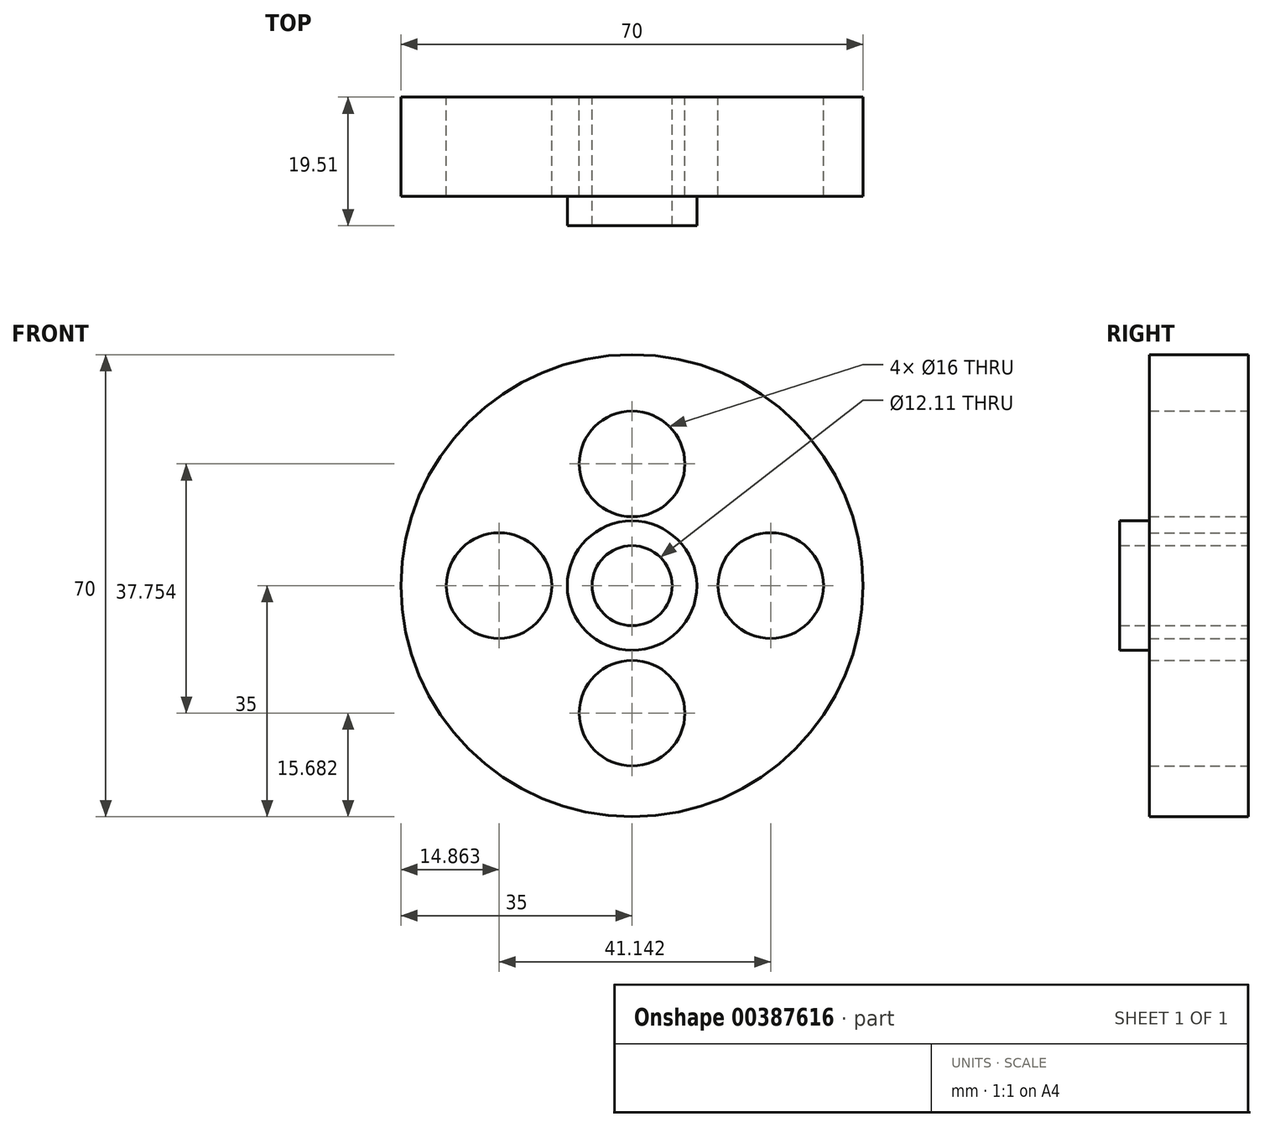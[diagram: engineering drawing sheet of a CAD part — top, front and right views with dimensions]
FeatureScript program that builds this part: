
annotation { "Feature Type Name" : "Feature", "Feature Type Description" : "" }
export const myFeature = defineFeature(function(context is Context, id is Id, definition is map)
    precondition{}
    {
        {
            var Q0;
            Q0=qCreatedBy(makeId("Front.planeOp"),FACE);
            var sketch = newSketch(context, id + "F0", { "sketchPlane" : qUnion([Q0])});
            skCircle(sketch, "E0", {"center": v(0, 0) * mm, "radius": 30 * mm});
            skCircle(sketch, "E1", {"center": v(0, 0) * mm, "radius": 35 * mm});
            skCircle(sketch, "E2", {"center": v(0, 0) * mm, "radius": 6.06 * mm});
            skCircle(sketch, "E3", {"center": v(0, 0) * mm, "radius": 9.81 * mm});
            skPoint(sketch, "E4", {"position": v(0, 18.44) * mm});
            skCircle(sketch, "E5", {"center": v(0, 18.44) * mm, "radius": 8 * mm});
            skPoint(sketch, "E6", {"position": v(21, 0) * mm});
            skCircle(sketch, "E7", {"center": v(21, 0) * mm, "radius": 8 * mm});
            skCircle(sketch, "E8", {"center": v(0, -19.32) * mm, "radius": 8 * mm});
            skCircle(sketch, "E9", {"center": v(-20.14, 0) * mm, "radius": 8 * mm});
            skSolve(sketch);
        }
        {
            var Q0;
            Q0=makeQuery(id+"F0.imprint","IMPRINT",FACE,{"disambiguationData":[TD([[makeQuery(id+"F0.imprint","IMPRINT",EDGE,{"derivedFrom":sQuery(id+"F0.wireOp",EDGE,"E0")}),-1.0]])]});
            extrude(context, id + "F1", {"entities" : qUnion([Q0]), "depth" : 15 * mm});
        }
        {
            var Q0;
            Q0=makeQuery(id+"F0.imprint","IMPRINT",FACE,{"disambiguationData":[TD([[makeQuery(id+"F0.imprint","IMPRINT",EDGE,{"derivedFrom":sQuery(id+"F0.wireOp",EDGE,"E0")}),1.0]])]});
            extrude(context, id + "F2", {"entities" : qUnion([Q0]), "operationType" : NewBodyOperationType.ADD, "depth" : 15 * mm});
        }
        {
            var Q0;
            Q0=makeQuery(id+"F0.imprint","IMPRINT",FACE,{"disambiguationData":[TD([[makeQuery(id+"F0.imprint","IMPRINT",EDGE,{"derivedFrom":sQuery(id+"F0.wireOp",EDGE,"E2")}),-1.0]])]});
            extrude(context, id + "F3", {"entities" : qUnion([Q0]), "operationType" : NewBodyOperationType.ADD, "depth" : 19.5 * mm});
        }
    });
